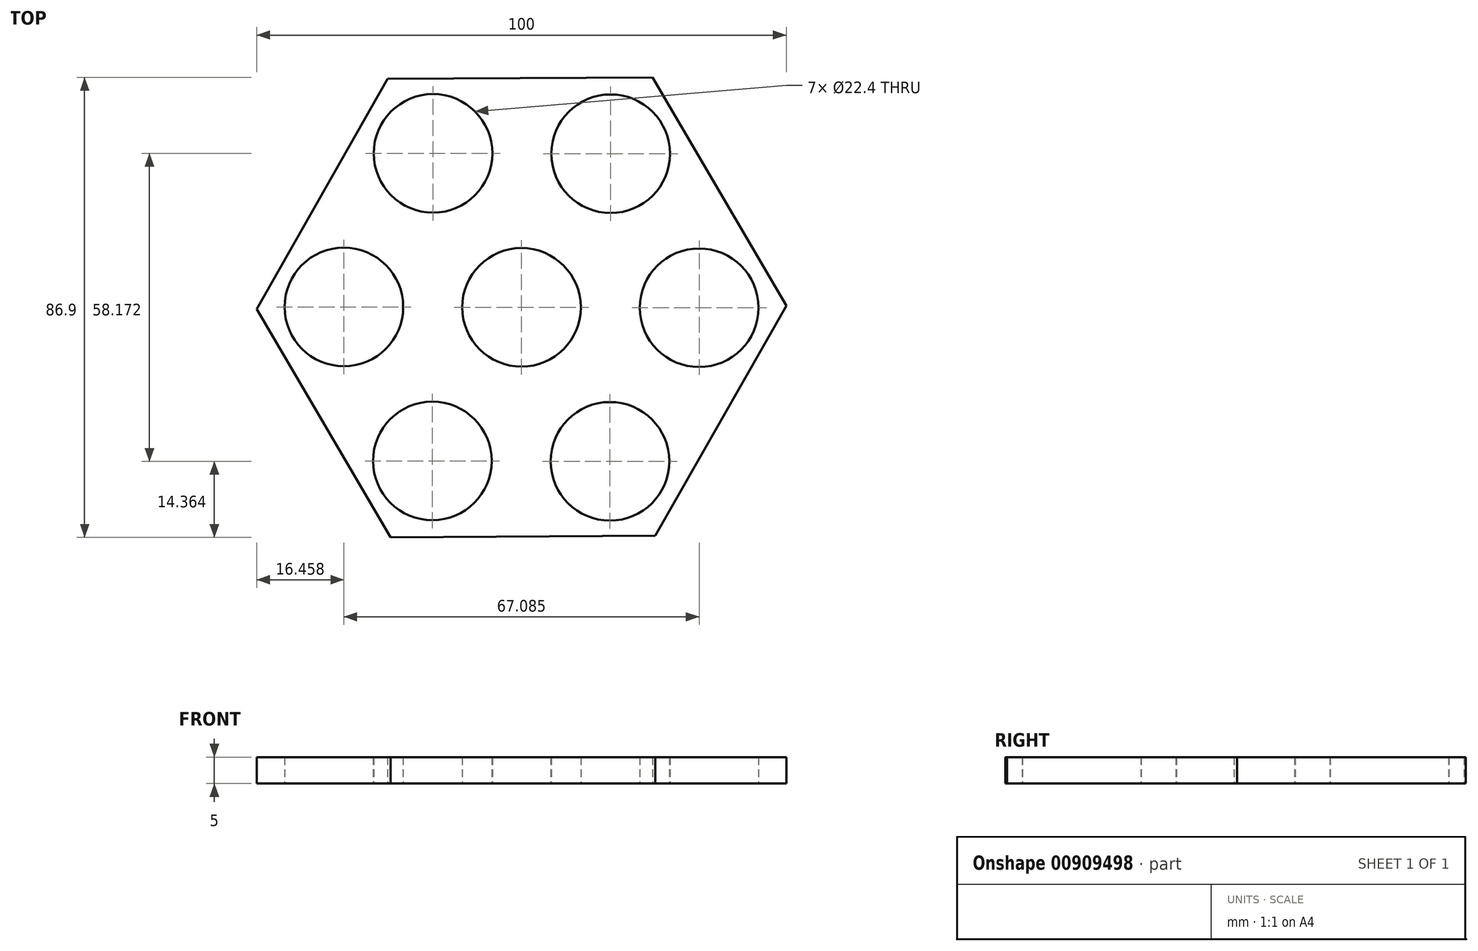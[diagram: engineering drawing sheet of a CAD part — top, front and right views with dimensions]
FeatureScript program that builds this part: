
annotation { "Feature Type Name" : "Feature", "Feature Type Description" : "" }
export const myFeature = defineFeature(function(context is Context, id is Id, definition is map)
    precondition{}
    {
        {
            var Q0;
            Q0=qCreatedBy(makeId("Top.planeOp"),FACE);
            var sketch = newSketch(context, id + "F0", { "sketchPlane" : qUnion([Q0])});
            skCircle(sketch, "E0", {"center": v(0, 0) * mm, "radius": 11.2 * mm});
            skCircle(sketch, "E1.cCircle", {"center": v(0, 0) * mm, "radius": 50 * mm, "construction": true});
            skLineSegment(sketch, "E1.0", {"start": v(24.74, 43.45) * mm, "end": v(50, 0.3) * mm});
            skLineSegment(sketch, "E1.1", {"start": v(50, 0.3) * mm, "end": v(25.26, -43.15) * mm});
            skLineSegment(sketch, "E1.2", {"start": v(25.26, -43.15) * mm, "end": v(-24.74, -43.45) * mm});
            skLineSegment(sketch, "E1.3", {"start": v(-24.74, -43.45) * mm, "end": v(-50, -0.3) * mm});
            skLineSegment(sketch, "E1.4", {"start": v(-50, -0.3) * mm, "end": v(-25.26, 43.15) * mm});
            skLineSegment(sketch, "E1.5", {"start": v(-25.26, 43.15) * mm, "end": v(24.74, 43.45) * mm});
            skCircle(sketch, "E2", {"center": v(33.54, -0.07) * mm, "radius": 11.2 * mm});
            skCircle(sketch, "E3.1.0", {"center": v(16.84, 29.01) * mm, "radius": 11.2 * mm});
            skCircle(sketch, "E3.2.0", {"center": v(-16.7, 29.09) * mm, "radius": 11.2 * mm});
            skCircle(sketch, "E3.3.0", {"center": v(-33.54, 0.07) * mm, "radius": 11.2 * mm});
            skCircle(sketch, "E3.4.0", {"center": v(-16.84, -29.01) * mm, "radius": 11.2 * mm});
            skCircle(sketch, "E3.5.0", {"center": v(16.7, -29.09) * mm, "radius": 11.2 * mm});
            skSolve(sketch);
        }
        {
            var Q0;
            Q0=makeQuery(id+"F0.imprint","IMPRINT",FACE,{"disambiguationData":[TD([[makeQuery(id+"F0.imprint","IMPRINT",EDGE,{"derivedFrom":sQuery(id+"F0.wireOp",EDGE,"E0")}),-1.0]])]});
            extrude(context, id + "F1", {"entities" : qUnion([Q0]), "depth" : 5 * mm, "offsetDistance" : 25 * mm});
        }
    });
